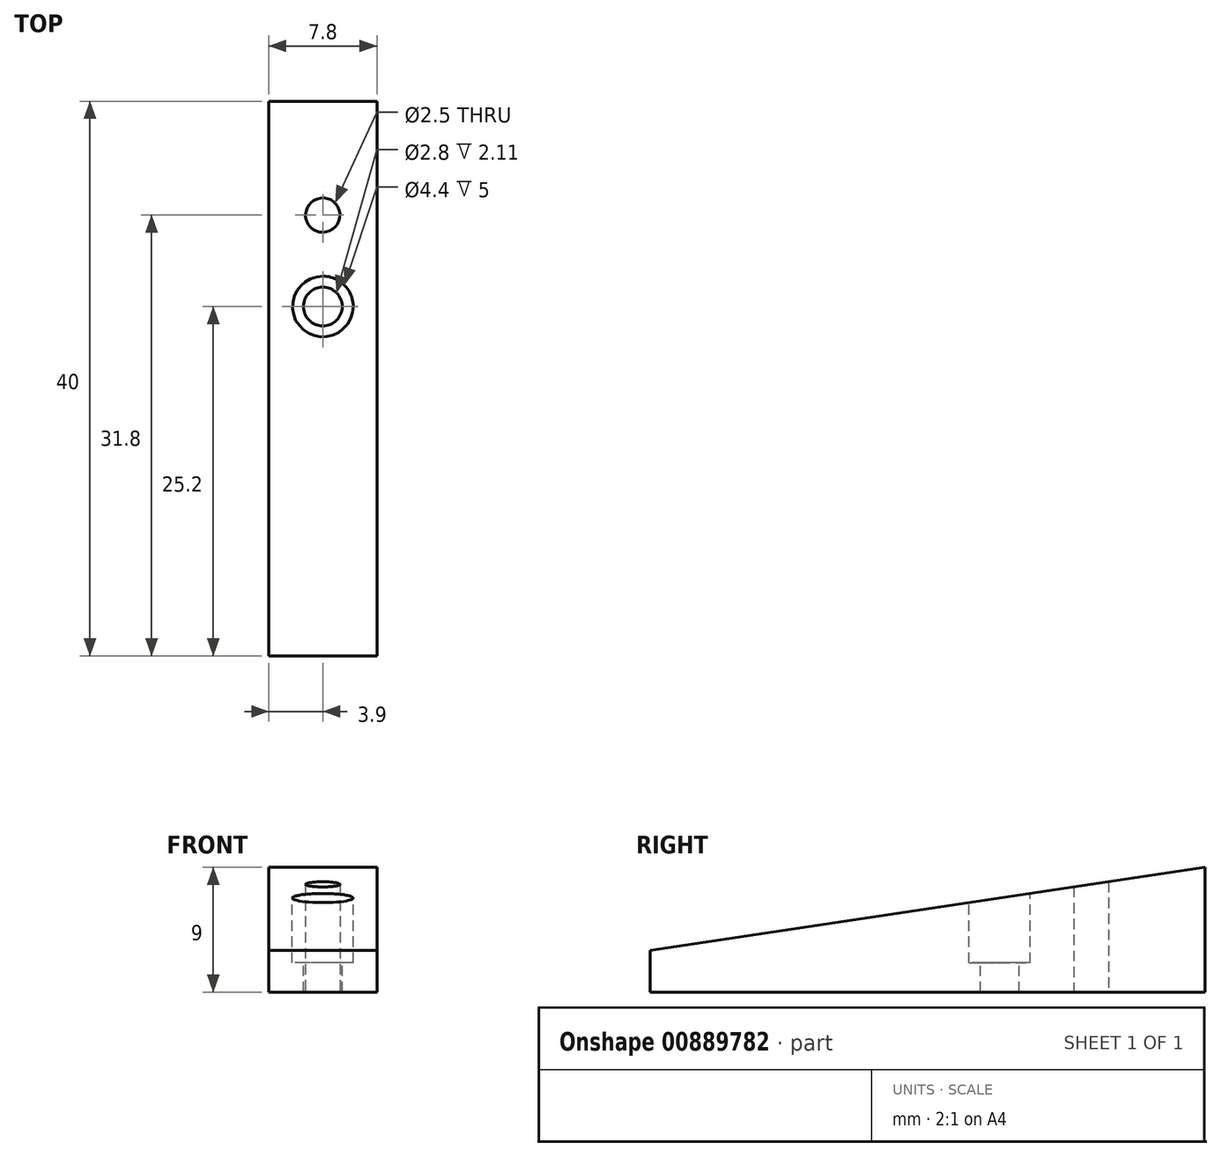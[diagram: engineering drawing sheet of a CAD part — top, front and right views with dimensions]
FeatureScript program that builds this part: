
annotation { "Feature Type Name" : "Feature", "Feature Type Description" : "" }
export const myFeature = defineFeature(function(context is Context, id is Id, definition is map)
    precondition{}
    {
        {
            var Q0;
            Q0=qCreatedBy(makeId("Right.planeOp"),FACE);
            var sketch = newSketch(context, id + "F0", { "sketchPlane" : qUnion([Q0])});
            skLineSegment(sketch, "E0", {"start": v(0, 0) * mm, "end": v(-40, 0) * mm});
            skLineSegment(sketch, "E1", {"start": v(0, 0) * mm, "end": v(0, 9) * mm});
            skLineSegment(sketch, "E2", {"start": v(-40, 0) * mm, "end": v(-40, 3) * mm});
            skLineSegment(sketch, "E3", {"start": v(-40, 3) * mm, "end": v(0, 9) * mm});
            skLineSegment(sketch, "E4", {"start": v(0, 0) * mm, "end": v(-7, 0) * mm, "construction": true});
            skLineSegment(sketch, "E5", {"start": v(-7, 0) * mm, "end": v(-7, 7.95) * mm});
            skLineSegment(sketch, "E6", {"start": v(-7, 0) * mm, "end": v(-9.4, 0) * mm});
            skLineSegment(sketch, "E7", {"start": v(-9.4, 0) * mm, "end": v(-9.4, 7.6) * mm});
            skLineSegment(sketch, "E8", {"start": v(-9.4, 0) * mm, "end": v(-13.4, 0) * mm, "construction": true});
            skLineSegment(sketch, "E9", {"start": v(-13.4, 0) * mm, "end": v(-16.2, 0) * mm});
            skLineSegment(sketch, "E10", {"start": v(-16.2, 0) * mm, "end": v(-16.2, 2.1) * mm});
            skLineSegment(sketch, "E11", {"start": v(-17, 4.11) * mm, "end": v(-17, 6.45) * mm});
            skLineSegment(sketch, "E12", {"start": v(-12.6, 4.11) * mm, "end": v(-12.6, 7.11) * mm});
            skLineSegment(sketch, "E13", {"start": v(-12.6, 7.11) * mm, "end": v(-12.6, 4.11) * mm});
            skPoint(sketch, "E14.orphan", {"position": v(-13.4, 6.99) * mm});
            skLineSegment(sketch, "E15", {"start": v(-13.4, 2.1) * mm, "end": v(-13.4, 0) * mm});
            skLineSegment(sketch, "E16", {"start": v(-8.2, 0) * mm, "end": v(-8.2, 7.77) * mm, "construction": true});
            skLineSegment(sketch, "E17", {"start": v(-14.8, 0) * mm, "end": v(-14.8, 6.78) * mm});
            skLineSegment(sketch, "E18", {"start": v(-12.6, 4.11) * mm, "end": v(-12.6, 2.1) * mm});
            skLineSegment(sketch, "E19", {"start": v(-17, 4.11) * mm, "end": v(-17, 2.1) * mm});
            skLineSegment(sketch, "E20", {"start": v(-12.6, 2.1) * mm, "end": v(-13.4, 2.1) * mm});
            skLineSegment(sketch, "E21.trimOffspring", {"start": v(-16.2, 2.1) * mm, "end": v(-17, 2.1) * mm});
            skSolve(sketch);
        }
        {
            var Q0;
            {var subQ0=sQuery(id+"F0.wireOp",EDGE,"E12");var subQ1=makeQuery(id+"F0.imprint","IMPRINT",EDGE,{"derivedFrom":subQ0});var subQ2=sQuery(id+"F0.wireOp",EDGE,"E7");var subQ3=makeQuery(id+"F0.imprint","IMPRINT",EDGE,{"derivedFrom":subQ2});var subQ16=sQuery(id+"F0.wireOp",EDGE,"E10");var subQ17=makeQuery(id+"F0.imprint","IMPRINT",EDGE,{"derivedFrom":subQ16});var subQ26=sQuery(id+"F0.wireOp",EDGE,"E1");var subQ27=sQuery(id+"F0.wireOp",EDGE,"E5");var subQ30=makeQuery(id+"F0.imprint","IMPRINT",EDGE,{"derivedFrom":subQ27});var subQ31=sQuery(id+"F0.wireOp",EDGE,"E2");Q0=qUnion([makeQuery(id+"F0.imprint","IMPRINT",FACE,{"disambiguationData":[TD([[subQ30,1.0]])]}),makeQuery(id+"F0.imprint","IMPRINT",FACE,{"disambiguationData":[TD([[makeQuery(id+"F0.imprint","IMPRINT",EDGE,{"derivedFrom":subQ31}),-1.0]])]}),makeQuery(id+"F0.imprint","IMPRINT",FACE,{"disambiguationData":[TD([[subQ1,1.0]])]}),makeQuery(id+"F0.imprint","IMPRINT",FACE,{"disambiguationData":[TD([[makeQuery(id+"F0.imprint","IMPRINT",EDGE,{"derivedFrom":subQ26}),1.0]])]}),makeQuery(id+"F0.imprint","IMPRINT",FACE,{"disambiguationData":[TD([[subQ17,-1.0]])]}),makeQuery(id+"F0.imprint","IMPRINT",FACE,{"disambiguationData":[TD([[subQ3,1.0]])]})]);}
            extrude(context, id + "F1", {"entities" : qUnion([Q0]), "endBound" : BoundingType.SYMMETRIC, "depth" : 7.8 * mm});
        }
        {
            var Q0;
            Q0=makeQuery(id+"F1.opExtrude","SWEPT_FACE",FACE,{"disambiguationData":[OSD([sQuery(id+"F0.wireOp",EDGE,"E0")])]});
            var sketch = newSketch(context, id + "F2", { "sketchPlane" : qUnion([Q0])});
            skCircle(sketch, "E22", {"center": v(0, 8.2) * mm, "radius": 1.25 * mm});
            skCircle(sketch, "E23", {"center": v(0, 14.8) * mm, "radius": 1.3 * mm});
            skSolve(sketch);
        }
        {
            var Q0;
            Q0=sQuery(id+"F2.wireOp",VERTEX,"E22.center");
            var Q1;
            Q1=makeQuery(id+"F1.opExtrude","SWEPT_BODY",BODY,{"disambiguationData":[OSD([sQuery(id+"F0.wireOp",EDGE,"E0"),sQuery(id+"F0.wireOp",EDGE,"E1"),sQuery(id+"F0.wireOp",EDGE,"E2"),sQuery(id+"F0.wireOp",EDGE,"E3")])]});
            hole(context, id + "F3", {"style" : HoleStyle.SIMPLE, "endStyle" : HoleEndStyle.BLIND, "holeDiameter" : 2.5 * mm, "holeDepth" : 12.7 * mm, "tappedDepth" : 12.7 * mm, "tapClearance" : 3, "locations" : qUnion([Q0]), "scope" : qUnion([Q1])});
        }
        {
            var Q0;
            Q0=sQuery(id+"F2.wireOp",VERTEX,"E23.center");
            var Q1;
            Q1=makeQuery(id+"F1.opExtrude","SWEPT_BODY",BODY,{"disambiguationData":[OSD([sQuery(id+"F0.wireOp",EDGE,"E0"),sQuery(id+"F0.wireOp",EDGE,"E1"),sQuery(id+"F0.wireOp",EDGE,"E2"),sQuery(id+"F0.wireOp",EDGE,"E3")])]});
            hole(context, id + "F4", {"style" : HoleStyle.SIMPLE, "endStyle" : HoleEndStyle.BLIND, "holeDiameter" : 2.5 * mm, "holeDepth" : 12.7 * mm, "tappedDepth" : 12.7 * mm, "tapClearance" : 3, "locations" : qUnion([Q0]), "scope" : qUnion([Q1])});
        }
        {
            var Q0;
            {var subQ0=sQuery(id+"F0.wireOp",EDGE,"E12");Q0=makeQuery(id+"F0.imprint","IMPRINT",FACE,{"disambiguationData":[TD([[makeQuery(id+"F0.imprint","IMPRINT",EDGE,{"derivedFrom":subQ0}),1.0]])]});}
            var Q1;
            Q1=sQuery(id+"F0.wireOp",EDGE,"E17");
            revolve(context, id + "F5", {"operationType" : NewBodyOperationType.REMOVE, "entities" : qUnion([Q0]), "axis" : qUnion([Q1]), "revolveType" : RevolveType.FULL, "oppositeDirection" : true});
        }
    });
